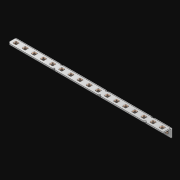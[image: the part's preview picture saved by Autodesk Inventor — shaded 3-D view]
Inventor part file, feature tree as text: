
AUTODESK INVENTOR PART (.ipt)
format: ipt  version: 2021 (Build 250183000, 183)  size: 693,760 bytes
history: native  units: in
note: dims shown in document units (in); Inventor stores cm internally (conversion verified against a paired STEP export)
features: extrude x35, other x34, sketch x3, pattern_linear x1, sheet_metal_op x1
ambient origin geometry x8: Origin, YZ Plane, XZ Plane, XY Plane, X Axis, Y Axis, Z Axis, Center Point
bodies: Solid1 (feature_tree)
feature tree (74):
  pattern_linear  "Rectangular Pattern1"  Spacing1=0.063in  [1 undecoded]
  extrude  "Extrusion1"  Depth=0.5in
  sketch  "Sketch1"  dims[d0=0.182in]
  other  "Srf1"
  sketch  "Sketch2"  dims[d1=0.063in d2=0.0in]
  other  "Srf2"
  other  "Srf3"
  other  "Srf5"
  other  "Srf7"
  other  "Srf9"
  other  "Srf11"
  other  "Srf13"
  other  "Srf15"
  other  "Srf17"
  other  "Srf19"
  other  "Srf21"
  other  "Srf23"
  other  "Srf25"
  other  "Srf27"
  other  "Srf29"
  other  "Srf31"
  other  "Srf33"
  other  "Srf4"
  other  "Srf6"
  other  "Srf8"
  other  "Srf10"
  other  "Srf12"
  other  "Srf14"
  other  "Srf16"
  other  "Srf18"
  other  "Srf20"
  other  "Srf22"
  other  "Srf24"
  other  "Srf26"
  other  "Srf28"
  other  "Srf30"
  other  "Srf32"
  other  "Srf34"
  sketch  "Sketch3"  dims[d3=0.182in d4=0.063in d5=0.0in d8=0.5in d9=9.0in d10=0.0in]
  sheet_metal_op  "Fold1"
  extrude  "ExtrusionSrf1"  Depth=0.5in TaperAngle=0.0deg
  extrude  "ExtrusionSrf2"  [1 undecoded]
  extrude  "ExtrusionSrf3"  [1 undecoded]
  extrude  "ExtrusionSrf4"  [1 undecoded]
  extrude  "ExtrusionSrf5"  [1 undecoded]
  extrude  "ExtrusionSrf6"  [1 undecoded]
  extrude  "ExtrusionSrf7"  [1 undecoded]
  extrude  "ExtrusionSrf8"  [1 undecoded]
  extrude  "ExtrusionSrf9"  [1 undecoded]
  extrude  "ExtrusionSrf10"  [1 undecoded]
  extrude  "ExtrusionSrf11"  [1 undecoded]
  extrude  "ExtrusionSrf12"  [1 undecoded]
  extrude  "ExtrusionSrf13"  [1 undecoded]
  extrude  "ExtrusionSrf14"  [1 undecoded]
  extrude  "ExtrusionSrf15"  [1 undecoded]
  extrude  "ExtrusionSrf16"  [1 undecoded]
  extrude  "ExtrusionSrf17"  [1 undecoded]
  extrude  "ExtrusionSrf18"  [1 undecoded]
  extrude  "ExtrusionSrf37"  [1 undecoded]
  extrude  "ExtrusionSrf38"  [1 undecoded]
  extrude  "ExtrusionSrf39"  [1 undecoded]
  extrude  "ExtrusionSrf40"  [1 undecoded]
  extrude  "ExtrusionSrf41"  [1 undecoded]
  extrude  "ExtrusionSrf42"  [1 undecoded]
  extrude  "ExtrusionSrf43"  [1 undecoded]
  extrude  "ExtrusionSrf44"  [1 undecoded]
  extrude  "ExtrusionSrf45"  [1 undecoded]
  extrude  "ExtrusionSrf46"  [1 undecoded]
  extrude  "ExtrusionSrf47"  [1 undecoded]
  extrude  "ExtrusionSrf48"  [1 undecoded]
  extrude  "ExtrusionSrf49"  [1 undecoded]
  extrude  "ExtrusionSrf50"  [1 undecoded]
  extrude  "ExtrusionSrf51"  [1 undecoded]
  extrude  "ExtrusionSrf52"  [1 undecoded]
note: 34 required parameter values undecoded (feature->parameter linkage not recoverable at this tier; creation-order binding heuristic only, values carry confidence <= 0.55)
